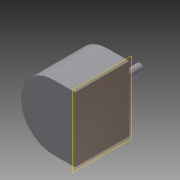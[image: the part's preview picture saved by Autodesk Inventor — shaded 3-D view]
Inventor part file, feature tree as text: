
AUTODESK INVENTOR PART (.ipt)
format: ipt  version: 2014 (Build 180170000, 170)  size: 78,848 bytes
history: native  units: in
note: dims shown in document units (in); Inventor stores cm internally (conversion verified against a paired STEP export)
features: other x3, sketch x2, plane x1
ambient origin geometry x8: Origin, YZ Plane, XZ Plane, XY Plane, X Axis, Y Axis, Z Axis, Center Point
bodies: Solid1 (feature_tree)
feature tree (6):
  other  "motor.ipt"
  other  "Solid1::motor.ipt"
  other  "TaggingFeature1"
  sketch  "Sketch1"  dims[d0=0.3937in]
  sketch  "Sketch2"  dims[d1=1.9685in d2=0.0in d3=0.2756in d4=0.7874in d5=0.0in]
  plane  "Work Plane1"
